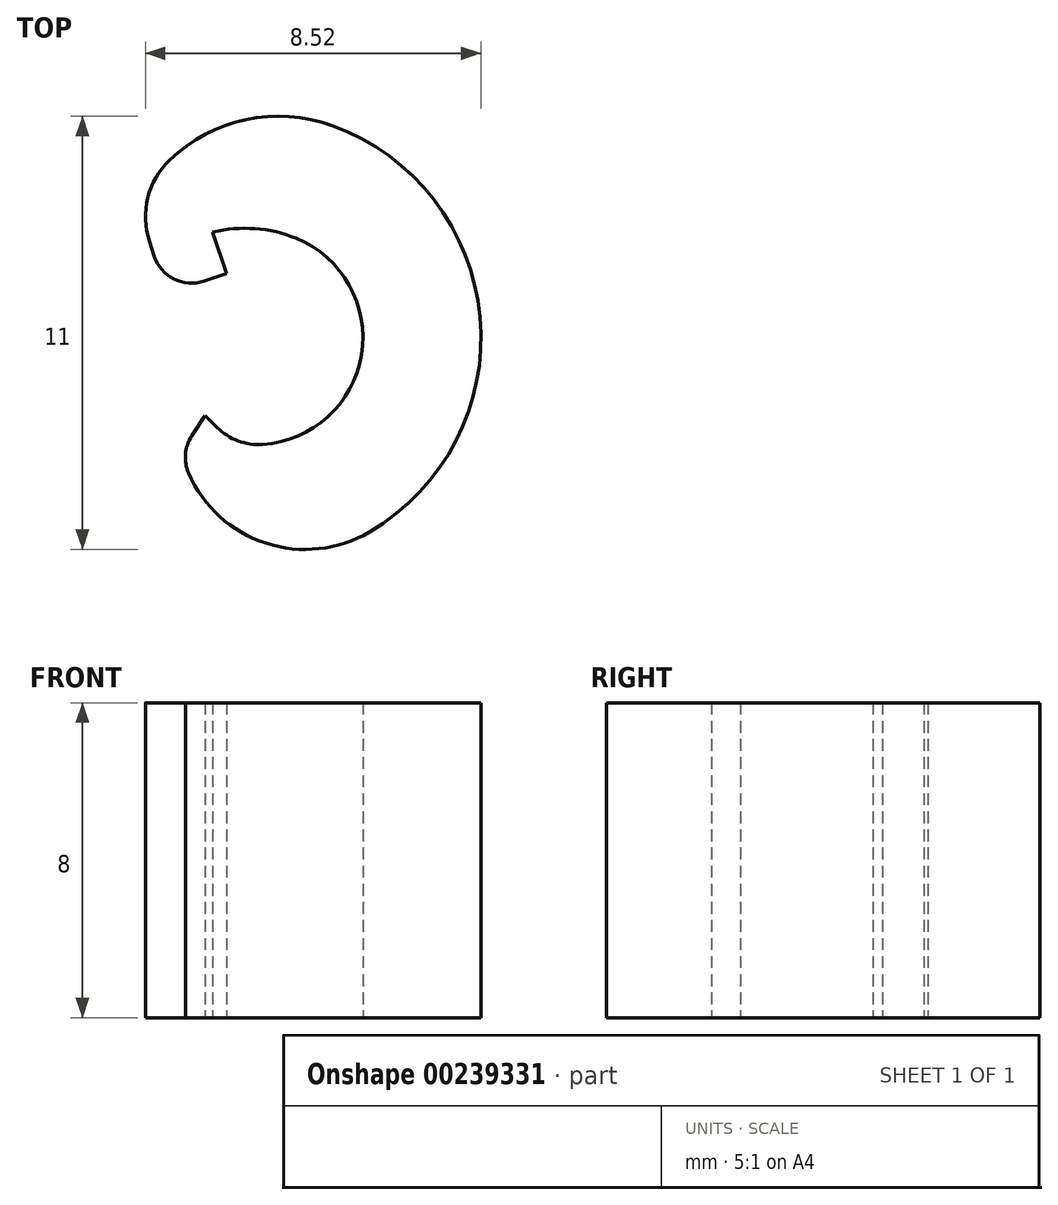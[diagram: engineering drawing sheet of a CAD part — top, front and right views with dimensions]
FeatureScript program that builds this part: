
annotation { "Feature Type Name" : "Feature", "Feature Type Description" : "" }
export const myFeature = defineFeature(function(context is Context, id is Id, definition is map)
    precondition{}
    {
        {
            var Q0;
            Q0=qCreatedBy(makeId("Top.planeOp"),FACE);
            var sketch = newSketch(context, id + "F0", { "sketchPlane" : qUnion([Q0])});
            skArc(sketch, "E0.0", {"start": v(0.18, -2.72) * mm, "mid": v(2.7, -0.37) * mm, "end": v(0.9, 2.57) * mm});
            skArc(sketch, "E1.0", {"start": v(2.9, -4.94) * mm, "mid": v(5.7, 0.52) * mm, "end": v(1.94, 5.39) * mm});
            skArc(sketch, "E2", {"start": v(-1.32, -2.27) * mm, "mid": v(2.61, -0.27) * mm, "end": v(-0.83, 2.5) * mm, "construction": true});
            skArc(sketch, "E3.0", {"start": v(-1.18, -1.83) * mm, "mid": v(2.16, -0.27) * mm, "end": v(-0.69, 2.06) * mm, "construction": true});
            skLineSegment(sketch, "E4", {"start": v(-0.69, 2.06) * mm, "end": v(-0.83, 2.5) * mm, "construction": true});
            skLineSegment(sketch, "E5", {"start": v(-0.74, 1.62) * mm, "end": v(-1.04, 2.52) * mm});
            skLineSegment(sketch, "E6", {"start": v(-0.74, 1.62) * mm, "end": v(-1.31, 1.43) * mm});
            skPoint(sketch, "E7.visualSharp", {"position": v(-3.67, 4.4) * mm});
            skArc(sketch, "E7.filletArc", {"start": v(1.94, 5.39) * mm, "mid": v(-0.25, 5.54) * mm, "end": v(-2.18, 4.5) * mm});
            skLineSegment(sketch, "E8", {"start": v(-1.28, -1.98) * mm, "end": v(-1.62, -2.5) * mm});
            skPoint(sketch, "E9.visualSharp", {"position": v(-3.12, -4.8) * mm});
            skLineSegment(sketch, "E10", {"start": v(-0.98, -2.28) * mm, "end": v(-1.28, -1.98) * mm});
            skArc(sketch, "E11.filletArc", {"start": v(-0.98, -2.28) * mm, "mid": v(-0.45, -2.63) * mm, "end": v(0.18, -2.72) * mm});
            skLineSegment(sketch, "E12", {"start": v(-1.04, 2.52) * mm, "end": v(-1.1, 2.68) * mm});
            skArc(sketch, "E13", {"start": v(1.03, 2.52) * mm, "mid": v(-0.02, 2.77) * mm, "end": v(-1.1, 2.68) * mm});
            skLineSegment(sketch, "E14", {"start": v(-2.57, 2.07) * mm, "end": v(-2.7, 2.43) * mm});
            skPoint(sketch, "E15.visualSharp", {"position": v(-2.26, 1.12) * mm});
            skArc(sketch, "E15.filletArc", {"start": v(-2.57, 2.07) * mm, "mid": v(-2.07, 1.49) * mm, "end": v(-1.31, 1.43) * mm});
            skPoint(sketch, "E16.visualSharp", {"position": v(-3.01, 3.38) * mm});
            skArc(sketch, "E16.filletArc", {"start": v(-2.18, 4.5) * mm, "mid": v(-2.74, 3.55) * mm, "end": v(-2.7, 2.43) * mm});
            skArc(sketch, "E17", {"start": v(-1.7, -3.45) * mm, "mid": v(0.26, -5.23) * mm, "end": v(2.9, -4.94) * mm});
            skPoint(sketch, "E18.visualSharp", {"position": v(-1.88, -2.9) * mm});
            skArc(sketch, "E18.filletArc", {"start": v(-1.62, -2.5) * mm, "mid": v(-1.78, -2.96) * mm, "end": v(-1.7, -3.45) * mm});
            skSolve(sketch);
        }
        {
            var Q0;
            Q0 = qSketchRegion(id + "F0", true);
            extrude(context, id + "F1", {"entities" : qUnion([Q0]), "depth" : 8 * mm});
        }
    });
